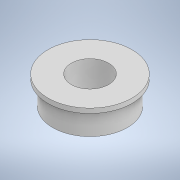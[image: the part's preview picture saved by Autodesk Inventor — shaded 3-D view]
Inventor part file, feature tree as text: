
AUTODESK INVENTOR PART (.ipt)
format: ipt  version: 2022 (Build 260153000, 153)  size: 112,128 bytes
history: native  units: mm
features: extrude x3, sketch x3, other x1
ambient origin geometry x8: Origin, YZ Plane, XZ Plane, XY Plane, X Axis, Y Axis, Z Axis, Center Point
bodies: Body1 (feature_tree)
feature tree (7):
  other  "ソリッド1"
  extrude  "押し出し1"  Depth=8.0mm
  extrude  "押し出し2"  Depth=2.5mm TaperAngle=0.0deg
  extrude  "押し出し3"  Depth=9.0mm
  sketch  "スケッチ1"
  sketch  "スケッチ2"
  sketch  "スケッチ3"
